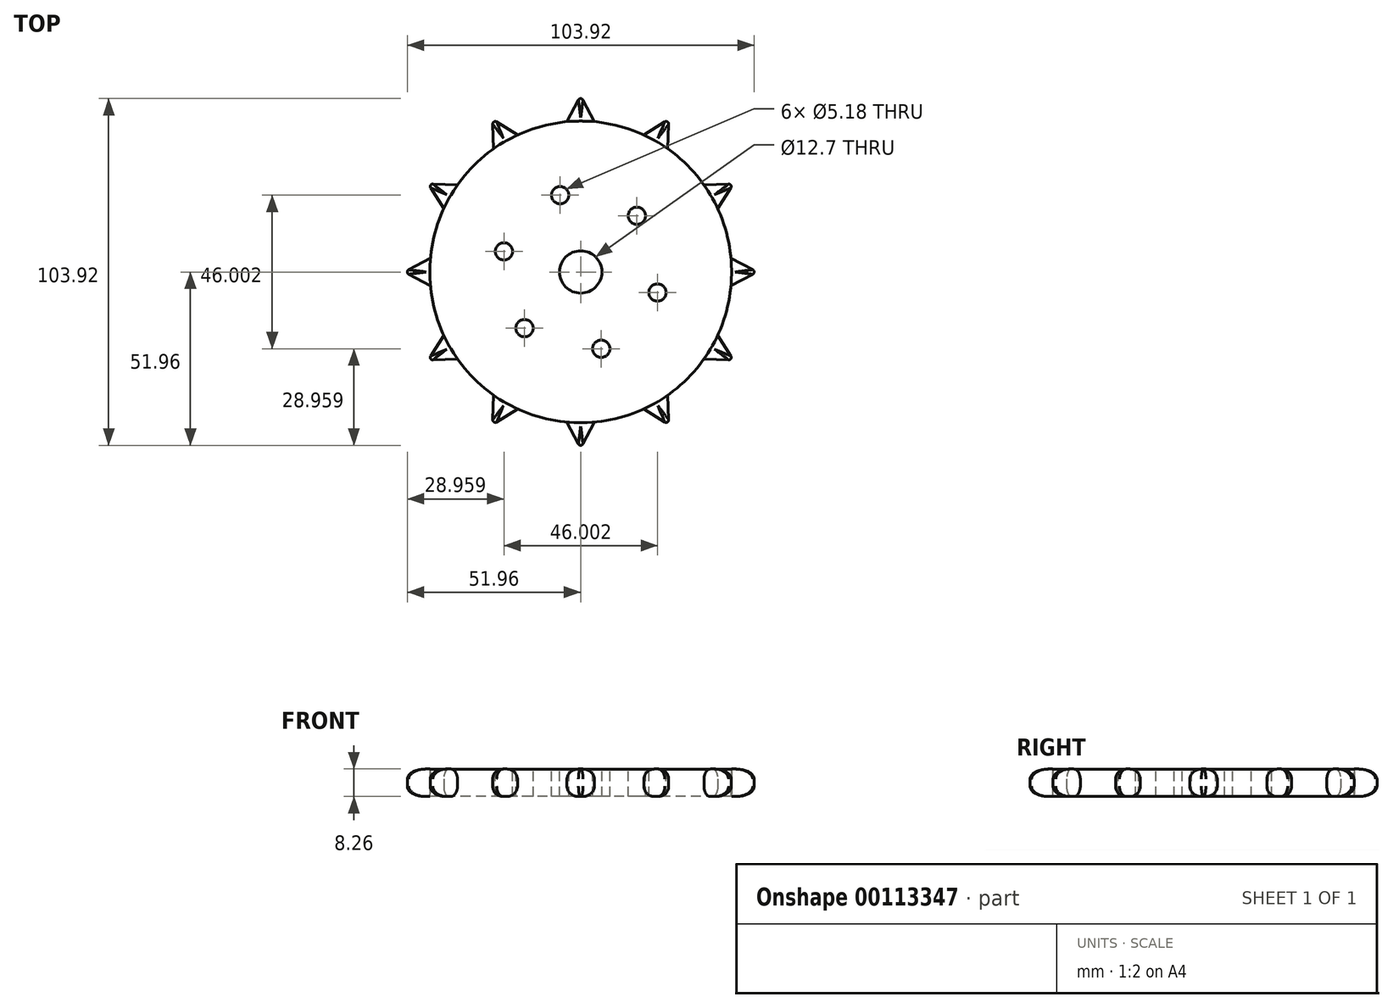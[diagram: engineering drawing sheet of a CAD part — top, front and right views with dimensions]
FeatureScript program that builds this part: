
annotation { "Feature Type Name" : "Feature", "Feature Type Description" : "" }
export const myFeature = defineFeature(function(context is Context, id is Id, definition is map)
    precondition{}
    {
        {
            var Q0;
            Q0=qCreatedBy(makeId("Top.planeOp"),FACE);
            var sketch = newSketch(context, id + "F0", { "sketchPlane" : qUnion([Q0])});
            skCircle(sketch, "E0", {"center": v(0, 0) * mm, "radius": 45.21 * mm});
            skSolve(sketch);
        }
        {
            var Q0;
            Q0 = qSketchRegion(id + "F0", true);
            extrude(context, id + "F1", {"entities" : qUnion([Q0]), "depth" : 8.23 * mm});
        }
        {
            var Q0;
            Q0=qCreatedBy(makeId("Top.planeOp"),FACE);
            var sketch = newSketch(context, id + "F2", { "sketchPlane" : qUnion([Q0])});
            skLineSegment(sketch, "E1", {"start": v(0, 0) * mm, "end": v(0, 52.83) * mm, "construction": true});
            skLineSegment(sketch, "E2.0", {"start": v(4.11, 0) * mm, "end": v(4.11, 54.4) * mm, "construction": true});
            skLineSegment(sketch, "E3.0", {"start": v(-4.11, 0) * mm, "end": v(-4.11, 54.4) * mm, "construction": true});
            skPoint(sketch, "E4", {"position": v(0, 45.21) * mm});
            skPoint(sketch, "E5", {"position": v(-4.11, 45.02) * mm});
            skPoint(sketch, "E6", {"position": v(4.11, 45.02) * mm});
            skLineSegment(sketch, "E7", {"start": v(0, 52.83) * mm, "end": v(-4.11, 45.02) * mm});
            skLineSegment(sketch, "E8", {"start": v(0, 52.83) * mm, "end": v(4.11, 45.02) * mm});
            skCircle(sketch, "E9", {"center": v(0, 0) * mm, "radius": 45.21 * mm});
            skSolve(sketch);
        }
        {
            var Q0;
            {var subQ0=sQuery(id+"F2.wireOp",EDGE,"E7");Q0=makeQuery(id+"F2.imprint","IMPRINT",FACE,{"disambiguationData":[TD([[makeQuery(id+"F2.imprint","IMPRINT",EDGE,{"derivedFrom":subQ0}),1.0]])]});}
            extrude(context, id + "F3", {"entities" : qUnion([Q0]), "depth" : 8.25 * mm});
        }
        {
            var Q0;
            Q0=makeQuery(id+"F3.opExtrude","SWEPT_EDGE",EDGE,{"disambiguationData":[OSD([sQuery(id+"F2.wireOp",EDGE,"E7"),sQuery(id+"F2.wireOp",EDGE,"E8")])]});
            fillet(context, id + "F4", {"entities" : qUnion([Q0]), "radius" : 0.76 * mm, "tangentPropagation" : true, "allowEdgeOverflow" : false});
        }
        {
            var Q0;
            Q0=makeQuery(id+"F3.opExtrude","CAP_EDGE",EDGE,{"disambiguationData":[OSD([sQuery(id+"F2.wireOp",EDGE,"E8")])],"isStart":false});
            var Q1;
            Q1=makeQuery(id+"F3.opExtrude","CAP_EDGE",EDGE,{"disambiguationData":[OSD([sQuery(id+"F2.wireOp",EDGE,"E8")])],"isStart":true});
            fillet(context, id + "F5", {"entities" : qUnion([Q0, Q1]), "radius" : 3.05 * mm, "tangentPropagation" : true, "allowEdgeOverflow" : false});
        }
        {
            var Q0;
            Q0=qCreatedBy(makeId("Front.planeOp"),FACE);
            var sketch = newSketch(context, id + "F6", { "sketchPlane" : qUnion([Q0])});
            skLineSegment(sketch, "E10", {"start": v(0, 0) * mm, "end": v(0, 19.65) * mm, "construction": true});
            skSolve(sketch);
        }
        {
            var Q0;
            Q0=makeQuery(id+"F3.opExtrude","SWEPT_BODY",BODY,{"disambiguationData":[OSD([sQuery(id+"F2.wireOp",EDGE,"E7"),sQuery(id+"F2.wireOp",EDGE,"E8"),sQuery(id+"F2.wireOp",EDGE,"E9")])]});
            var Q1;
            Q1=sQuery(id+"F6.wireOp",EDGE,"E10");
            circularPattern(context, id + "F7", {"entities" : qUnion([Q0]), "axis" : qUnion([Q1]), "angle" : 360 * degree, "instanceCount" : 12, "equalSpace" : true});
        }
        {
            var Q0;
            Q0=makeQuery(id+"F1.opExtrude","CAP_FACE",FACE,{"disambiguationData":[OSD([sQuery(id+"F0.wireOp",EDGE,"E0")])],"isStart":false});
            var sketch = newSketch(context, id + "F8", { "sketchPlane" : qUnion([Q0])});
            skLineSegment(sketch, "E11", {"start": v(0, 0) * mm, "end": v(0, 60.06) * mm, "construction": true});
            skLineSegment(sketch, "E12", {"start": v(0, 0) * mm, "end": v(-13.99, 52.2) * mm, "construction": true});
            skCircle(sketch, "E13", {"center": v(0, 0) * mm, "radius": 23.81 * mm, "construction": true});
            skCircle(sketch, "E14", {"center": v(-6.16, 23) * mm, "radius": 2.6 * mm});
            skCircle(sketch, "E15.1.0", {"center": v(-23, 6.16) * mm, "radius": 2.6 * mm});
            skCircle(sketch, "E15.2.0", {"center": v(-16.84, -16.84) * mm, "radius": 2.6 * mm});
            skCircle(sketch, "E16.1.3.0", {"center": v(6.16, -23) * mm, "radius": 2.6 * mm});
            skCircle(sketch, "E16.1.4.0", {"center": v(23, -6.16) * mm, "radius": 2.6 * mm});
            skCircle(sketch, "E16.1.5.0", {"center": v(16.84, 16.84) * mm, "radius": 2.6 * mm});
            skLineSegment(sketch, "E17", {"start": v(0, 0) * mm, "end": v(16.84, 16.84) * mm, "construction": true});
            skSolve(sketch);
        }
        {
            var Q0;
            Q0=makeQuery(id+"F8.imprint","IMPRINT",FACE,{"disambiguationData":[TD([[makeQuery(id+"F8.imprint","IMPRINT",EDGE,{"derivedFrom":sQuery(id+"F8.wireOp",EDGE,"E14")}),1.0]])]});
            var Q1;
            Q1=makeQuery(id+"F8.imprint","IMPRINT",FACE,{"disambiguationData":[TD([[makeQuery(id+"F8.imprint","IMPRINT",EDGE,{"derivedFrom":sQuery(id+"F8.wireOp",EDGE,"E15.1.0")}),1.0]])]});
            var Q2;
            Q2=makeQuery(id+"F8.imprint","IMPRINT",FACE,{"disambiguationData":[TD([[makeQuery(id+"F8.imprint","IMPRINT",EDGE,{"derivedFrom":sQuery(id+"F8.wireOp",EDGE,"E15.2.0")}),1.0]])]});
            var Q3;
            Q3=makeQuery(id+"F8.imprint","IMPRINT",FACE,{"disambiguationData":[TD([[makeQuery(id+"F8.imprint","IMPRINT",EDGE,{"derivedFrom":sQuery(id+"F8.wireOp",EDGE,"E16.1.3.0")}),1.0]])]});
            var Q4;
            Q4=makeQuery(id+"F8.imprint","IMPRINT",FACE,{"disambiguationData":[TD([[makeQuery(id+"F8.imprint","IMPRINT",EDGE,{"derivedFrom":sQuery(id+"F8.wireOp",EDGE,"E16.1.4.0")}),1.0]])]});
            var Q5;
            Q5=makeQuery(id+"F8.imprint","IMPRINT",FACE,{"disambiguationData":[TD([[makeQuery(id+"F8.imprint","IMPRINT",EDGE,{"derivedFrom":sQuery(id+"F8.wireOp",EDGE,"E16.1.5.0")}),1.0]])]});
            extrude(context, id + "F9", {"entities" : qUnion([Q0, Q1, Q2, Q3, Q4, Q5]), "operationType" : NewBodyOperationType.REMOVE, "oppositeDirection" : true, "depth" : 25.4 * mm});
        }
        {
            var Q0;
            Q0=makeQuery(id+"F8.imprint","IMPRINT",FACE,{"disambiguationData":[TD([[makeQuery(id+"F8.imprint","IMPRINT",EDGE,{"derivedFrom":sQuery(id+"F8.wireOp",EDGE,"E14")}),-1.0]])]});
            var sketch = newSketch(context, id + "F10", { "sketchPlane" : qUnion([Q0])});
            skCircle(sketch, "E18", {"center": v(0, 0) * mm, "radius": 6.35 * mm});
            skSolve(sketch);
        }
        {
            var Q0;
            Q0 = qSketchRegion(id + "F10", true);
            extrude(context, id + "F11", {"entities" : qUnion([Q0]), "operationType" : NewBodyOperationType.REMOVE, "oppositeDirection" : true, "depth" : 25.4 * mm});
        }
    });
